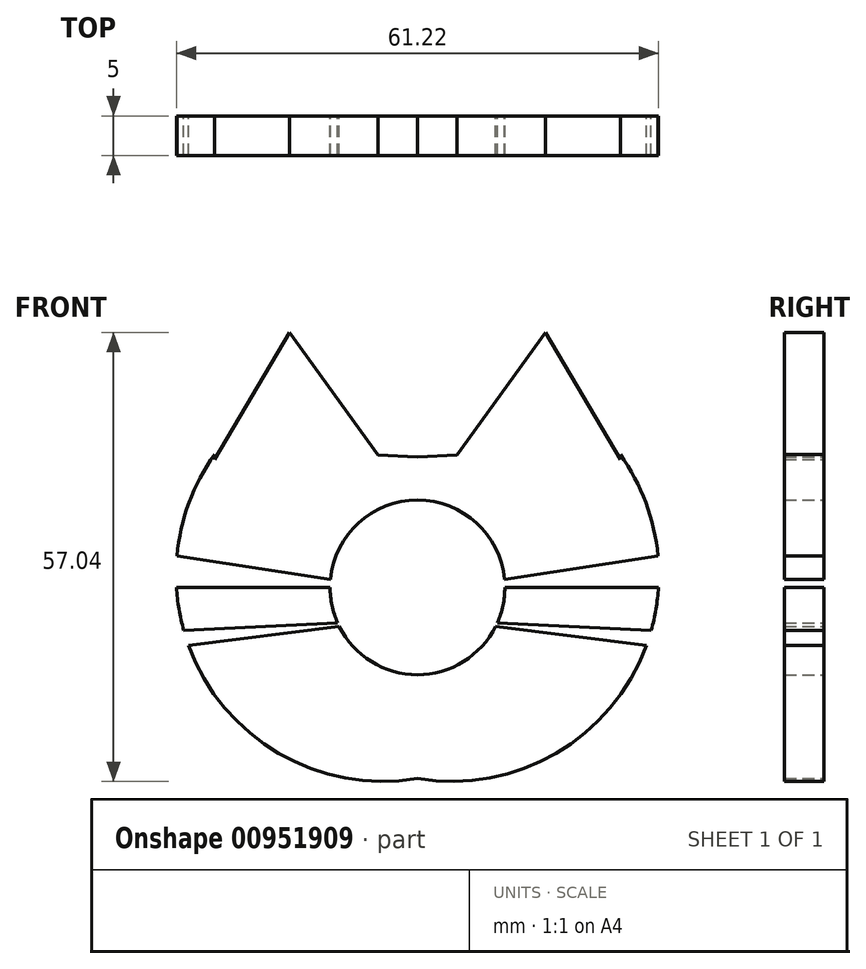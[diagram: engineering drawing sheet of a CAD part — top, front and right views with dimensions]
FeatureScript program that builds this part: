
annotation { "Feature Type Name" : "Feature", "Feature Type Description" : "" }
export const myFeature = defineFeature(function(context is Context, id is Id, definition is map)
    precondition{}
    {
        {
            var Q0;
            Q0=qCreatedBy(makeId("Front.planeOp"),FACE);
            var sketch = newSketch(context, id + "F0", { "sketchPlane" : qUnion([Q0])});
            skCircle(sketch, "E0", {"center": v(0, 0) * mm, "radius": 11.1 * mm});
            skSolve(sketch);
        }
        {
            var Q0;
            Q0=qCreatedBy(makeId("Front.planeOp"),FACE);
            var sketch = newSketch(context, id + "F1", { "sketchPlane" : qUnion([Q0])});
            skLineSegment(sketch, "E1", {"start": v(5.04, 16.84) * mm, "end": v(16.26, 32.38) * mm});
            skLineSegment(sketch, "E2", {"start": v(16.26, 32.38) * mm, "end": v(25.76, 16.26) * mm});
            skLineSegment(sketch, "E3", {"start": v(5.04, 16.84) * mm, "end": v(-5.04, 16.26) * mm});
            skArc(sketch, "E4", {"start": v(0, -24.29) * mm, "mid": v(26.66, -12.33) * mm, "end": v(25.76, 16.89) * mm});
            skLineSegment(sketch, "E5", {"start": v(25.76, 16.89) * mm, "end": v(25.76, 16.26) * mm});
            skLineSegment(sketch, "E6", {"start": v(4.46, 0) * mm, "end": v(37.27, 5.04) * mm});
            skLineSegment(sketch, "E7", {"start": v(3.89, -4.17) * mm, "end": v(38.13, -8.5) * mm});
            skLineSegment(sketch, "E8", {"start": v(38.13, -8.5) * mm, "end": v(38.13, -5.9) * mm});
            skLineSegment(sketch, "E9", {"start": v(38.13, -5.9) * mm, "end": v(3.89, -4.17) * mm});
            skLineSegment(sketch, "E10", {"start": v(37.27, 5.04) * mm, "end": v(38.04, 0) * mm});
            skLineSegment(sketch, "E11", {"start": v(38.04, 0) * mm, "end": v(4.46, 0) * mm});
            skFitSpline(sketch, "E12", {"points": [v(2.73, -24.6) * mm, v(-4.17, -28.35) * mm, v(-4.17, -28.06) * mm], "startDerivative": vector(-14.22, -5.42) * mm, "endDerivative": vector(0.76, 2.28) * mm});
            skLineSegment(sketch, "E13.MirrorCS", {"start": v(-25.76, 16.89) * mm, "end": v(-25.76, 16.26) * mm});
            skLineSegment(sketch, "E14.MirrorCS", {"start": v(-37.27, 5.04) * mm, "end": v(-38.04, 0) * mm});
            skLineSegment(sketch, "E15.MirrorCS", {"start": v(-38.13, -8.5) * mm, "end": v(-38.13, -5.9) * mm});
            skFitSpline(sketch, "E16.MirrorCS", {"points": [v(-2.73, -24.6) * mm, v(4.17, -28.35) * mm, v(4.17, -28.06) * mm], "startDerivative": vector(14.22, -5.42) * mm, "endDerivative": vector(-0.76, 2.28) * mm});
            skLineSegment(sketch, "E17.MirrorCS", {"start": v(-4.46, 0) * mm, "end": v(-37.27, 5.04) * mm});
            skLineSegment(sketch, "E18.MirrorCS", {"start": v(-16.26, 32.38) * mm, "end": v(-25.76, 16.26) * mm});
            skLineSegment(sketch, "E19.MirrorCS", {"start": v(-38.04, 0) * mm, "end": v(-4.46, 0) * mm});
            skLineSegment(sketch, "E20.MirrorCS", {"start": v(-3.89, -4.17) * mm, "end": v(-38.13, -8.5) * mm});
            skArc(sketch, "E21.MirrorCS", {"start": v(0, -24.29) * mm, "mid": v(-26.66, -12.33) * mm, "end": v(-25.76, 16.89) * mm});
            skLineSegment(sketch, "E22.MirrorCS", {"start": v(-5.04, 16.84) * mm, "end": v(5.04, 16.26) * mm});
            skLineSegment(sketch, "E23.MirrorCS", {"start": v(-5.04, 16.84) * mm, "end": v(-16.26, 32.38) * mm});
            skLineSegment(sketch, "E24.MirrorCS", {"start": v(-38.13, -5.9) * mm, "end": v(-3.89, -4.17) * mm});
            skSolve(sketch);
        }
        {
            var Q0;
            {var subQ25=sQuery(id+"F1.wireOp",EDGE,"E1");Q0=makeQuery(id+"F1.imprint","IMPRINT",FACE,{"disambiguationData":[TD([[makeQuery(id+"F1.imprint","IMPRINT",EDGE,{"derivedFrom":subQ25}),-1.0]])]});}
            extrude(context, id + "F2", {"entities" : qUnion([Q0]), "depth" : 5 * mm, "offsetDistance" : 25 * mm});
        }
        {
            var Q0;
            Q0 = qSketchRegion(id + "F0", true);
            extrude(context, id + "F3", {"entities" : qUnion([Q0]), "operationType" : NewBodyOperationType.REMOVE, "depth" : 25 * mm, "offsetDistance" : 25 * mm});
        }
    });
